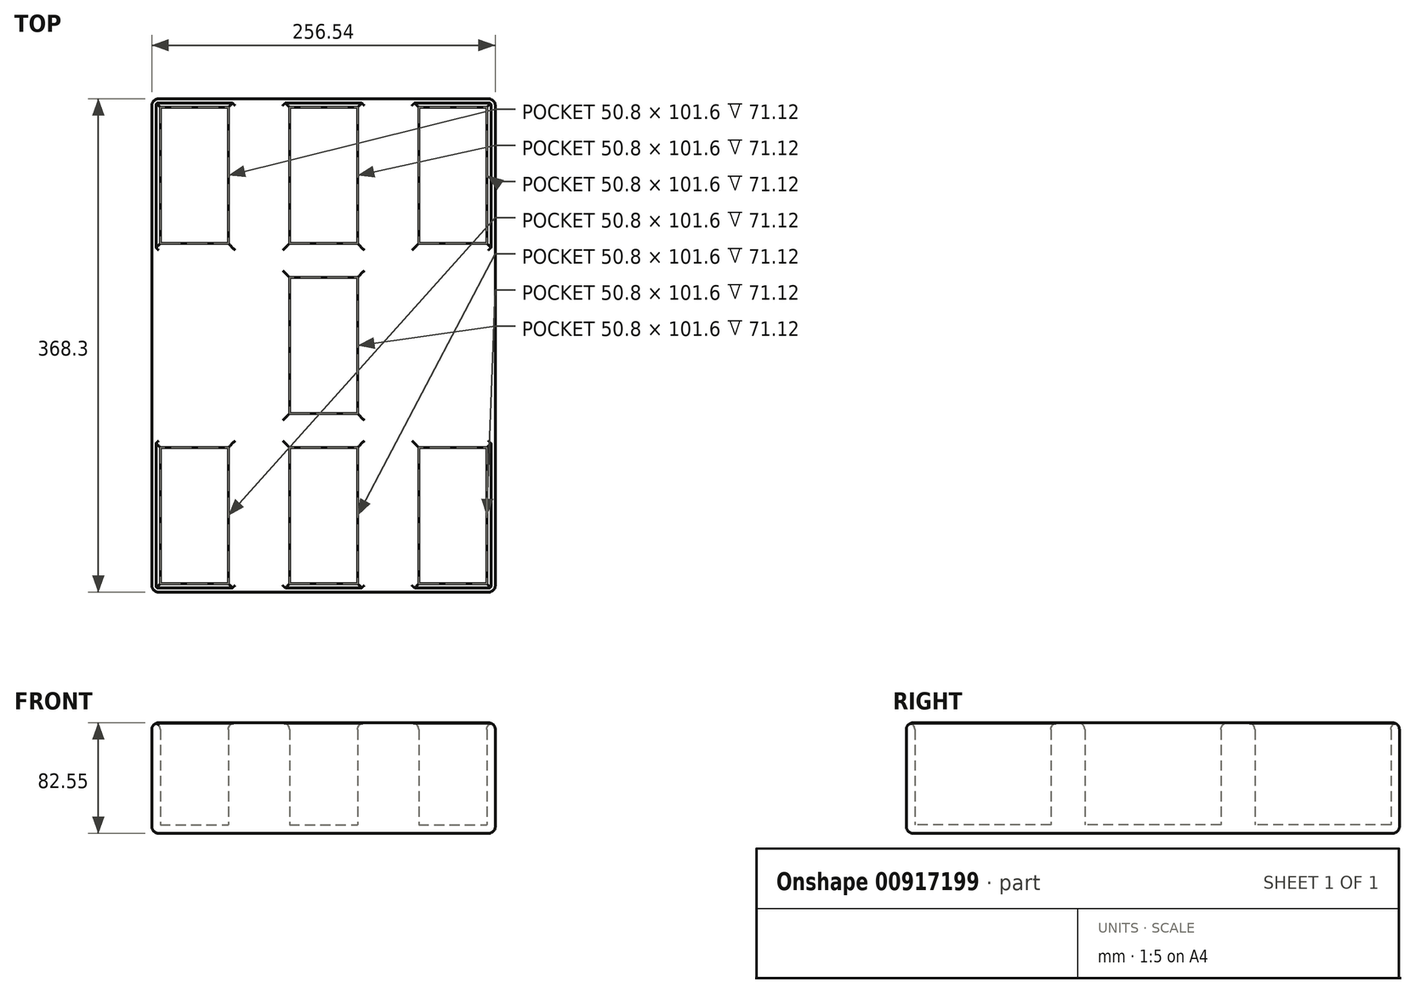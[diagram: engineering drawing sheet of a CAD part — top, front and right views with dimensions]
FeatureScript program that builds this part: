
annotation { "Feature Type Name" : "Feature", "Feature Type Description" : "" }
export const myFeature = defineFeature(function(context is Context, id is Id, definition is map)
    precondition{}
    {
        {
            var Q0;
            Q0=qCreatedBy(makeId("Top.planeOp"),FACE);
            var sketch = newSketch(context, id + "F0", { "sketchPlane" : qUnion([Q0])});
            skLineSegment(sketch, "E0.bottom", {"start": v(-193.27, 101.6) * mm, "end": v(-142.47, 101.6) * mm});
            skLineSegment(sketch, "E0.top", {"start": v(-193.27, 0) * mm, "end": v(-142.47, 0) * mm});
            skLineSegment(sketch, "E0.left", {"start": v(-193.27, 101.6) * mm, "end": v(-193.27, 0) * mm});
            skLineSegment(sketch, "E0.right", {"start": v(-142.47, 101.6) * mm, "end": v(-142.47, 0) * mm});
            skLineSegment(sketch, "E1.bottom", {"start": v(-96.75, 101.6) * mm, "end": v(-45.95, 101.6) * mm});
            skLineSegment(sketch, "E1.top", {"start": v(-96.75, 0) * mm, "end": v(-45.95, 0) * mm});
            skLineSegment(sketch, "E1.left", {"start": v(-96.75, 101.6) * mm, "end": v(-96.75, 0) * mm});
            skLineSegment(sketch, "E1.right", {"start": v(-45.95, 101.6) * mm, "end": v(-45.95, 0) * mm});
            skLineSegment(sketch, "E2.bottom", {"start": v(-0.23, 101.6) * mm, "end": v(50.57, 101.6) * mm});
            skLineSegment(sketch, "E2.top", {"start": v(-0.23, 0) * mm, "end": v(50.57, 0) * mm});
            skLineSegment(sketch, "E2.left", {"start": v(-0.23, 101.6) * mm, "end": v(-0.23, 0) * mm});
            skLineSegment(sketch, "E2.right", {"start": v(50.57, 101.6) * mm, "end": v(50.57, 0) * mm});
            skLineSegment(sketch, "E3.bottom", {"start": v(-193.27, -152.4) * mm, "end": v(-142.47, -152.4) * mm});
            skLineSegment(sketch, "E3.top", {"start": v(-193.27, -254) * mm, "end": v(-142.47, -254) * mm});
            skLineSegment(sketch, "E3.left", {"start": v(-193.27, -152.4) * mm, "end": v(-193.27, -254) * mm});
            skLineSegment(sketch, "E3.right", {"start": v(-142.47, -152.4) * mm, "end": v(-142.47, -254) * mm});
            skLineSegment(sketch, "E4.bottom", {"start": v(-96.75, -152.4) * mm, "end": v(-45.95, -152.4) * mm});
            skLineSegment(sketch, "E4.top", {"start": v(-96.75, -254) * mm, "end": v(-45.95, -254) * mm});
            skLineSegment(sketch, "E4.left", {"start": v(-96.75, -152.4) * mm, "end": v(-96.75, -254) * mm});
            skLineSegment(sketch, "E4.right", {"start": v(-45.95, -152.4) * mm, "end": v(-45.95, -254) * mm});
            skLineSegment(sketch, "E5.bottom", {"start": v(-0.23, -152.4) * mm, "end": v(50.57, -152.4) * mm});
            skLineSegment(sketch, "E5.top", {"start": v(-0.23, -254) * mm, "end": v(50.57, -254) * mm});
            skLineSegment(sketch, "E5.left", {"start": v(-0.23, -152.4) * mm, "end": v(-0.23, -254) * mm});
            skLineSegment(sketch, "E5.right", {"start": v(50.57, -152.4) * mm, "end": v(50.57, -254) * mm});
            skLineSegment(sketch, "E6.bottom", {"start": v(-96.75, -25.4) * mm, "end": v(-45.95, -25.4) * mm});
            skLineSegment(sketch, "E6.top", {"start": v(-96.75, -127) * mm, "end": v(-45.95, -127) * mm});
            skLineSegment(sketch, "E6.left", {"start": v(-96.75, -25.4) * mm, "end": v(-96.75, -127) * mm});
            skLineSegment(sketch, "E6.right", {"start": v(-45.95, -25.4) * mm, "end": v(-45.95, -127) * mm});
            skLineSegment(sketch, "E7.0", {"start": v(-199.62, 107.95) * mm, "end": v(-142.47, 107.95) * mm});
            skLineSegment(sketch, "E7.1", {"start": v(-199.62, 107.95) * mm, "end": v(-199.62, 0) * mm});
            skLineSegment(sketch, "E8.0", {"start": v(-199.62, -260.35) * mm, "end": v(-142.47, -260.35) * mm});
            skLineSegment(sketch, "E8.1", {"start": v(-199.62, -152.4) * mm, "end": v(-199.62, -260.35) * mm});
            skLineSegment(sketch, "E9.0", {"start": v(-0.23, -260.35) * mm, "end": v(56.92, -260.35) * mm});
            skLineSegment(sketch, "E9.1", {"start": v(56.92, -152.4) * mm, "end": v(56.92, -260.35) * mm});
            skLineSegment(sketch, "E10.0", {"start": v(56.92, 107.95) * mm, "end": v(56.92, 12.7) * mm});
            skLineSegment(sketch, "E10.1", {"start": v(-0.23, 107.95) * mm, "end": v(56.92, 107.95) * mm});
            skLineSegment(sketch, "E11", {"start": v(-142.47, 107.95) * mm, "end": v(-0.23, 107.95) * mm});
            skLineSegment(sketch, "E12", {"start": v(-199.62, 0) * mm, "end": v(-199.62, -152.4) * mm});
            skLineSegment(sketch, "E13", {"start": v(-142.47, -260.35) * mm, "end": v(-0.23, -260.35) * mm});
            skLineSegment(sketch, "E14", {"start": v(56.92, 12.7) * mm, "end": v(56.92, -152.4) * mm});
            skSolve(sketch);
        }
        {
            var Q0;
            Q0=makeQuery(id+"F0.imprint","IMPRINT",FACE,{"disambiguationData":[TD([[makeQuery(id+"F0.imprint","IMPRINT",EDGE,{"derivedFrom":sQuery(id+"F0.wireOp",EDGE,"E0.bottom")}),1.0]])]});
            extrude(context, id + "F1", {"entities" : qUnion([Q0]), "depth" : 82.55 * mm, "offsetDistance" : 25.4 * mm});
        }
        {
            var Q0;
            Q0=makeQuery(id+"F0.imprint","IMPRINT",FACE,{"disambiguationData":[TD([[makeQuery(id+"F0.imprint","IMPRINT",EDGE,{"derivedFrom":sQuery(id+"F0.wireOp",EDGE,"E0.bottom")}),-1.0]])]});
            var Q1;
            Q1=makeQuery(id+"F0.imprint","IMPRINT",FACE,{"disambiguationData":[TD([[makeQuery(id+"F0.imprint","IMPRINT",EDGE,{"derivedFrom":sQuery(id+"F0.wireOp",EDGE,"E1.bottom")}),-1.0]])]});
            var Q2;
            Q2=makeQuery(id+"F0.imprint","IMPRINT",FACE,{"disambiguationData":[TD([[makeQuery(id+"F0.imprint","IMPRINT",EDGE,{"derivedFrom":sQuery(id+"F0.wireOp",EDGE,"E2.bottom")}),-1.0]])]});
            var Q3;
            Q3=makeQuery(id+"F0.imprint","IMPRINT",FACE,{"disambiguationData":[TD([[makeQuery(id+"F0.imprint","IMPRINT",EDGE,{"derivedFrom":sQuery(id+"F0.wireOp",EDGE,"E6.bottom")}),-1.0]])]});
            var Q4;
            Q4=makeQuery(id+"F0.imprint","IMPRINT",FACE,{"disambiguationData":[TD([[makeQuery(id+"F0.imprint","IMPRINT",EDGE,{"derivedFrom":sQuery(id+"F0.wireOp",EDGE,"E3.bottom")}),-1.0]])]});
            var Q5;
            Q5=makeQuery(id+"F0.imprint","IMPRINT",FACE,{"disambiguationData":[TD([[makeQuery(id+"F0.imprint","IMPRINT",EDGE,{"derivedFrom":sQuery(id+"F0.wireOp",EDGE,"E4.bottom")}),-1.0]])]});
            var Q6;
            Q6=makeQuery(id+"F0.imprint","IMPRINT",FACE,{"disambiguationData":[TD([[makeQuery(id+"F0.imprint","IMPRINT",EDGE,{"derivedFrom":sQuery(id+"F0.wireOp",EDGE,"E5.bottom")}),-1.0]])]});
            extrude(context, id + "F2", {"entities" : qUnion([Q0, Q1, Q2, Q3, Q4, Q5, Q6]), "operationType" : NewBodyOperationType.ADD, "depth" : 6.35 * mm, "offsetDistance" : 25.4 * mm});
        }
        {
            var Q0;
            Q0=makeQuery(id+"F1.opExtrude","CAP_FACE",FACE,{"disambiguationData":[OSD([sQuery(id+"F0.wireOp",EDGE,"E0.bottom"),sQuery(id+"F0.wireOp",EDGE,"E0.top"),sQuery(id+"F0.wireOp",EDGE,"E0.left"),sQuery(id+"F0.wireOp",EDGE,"E0.right"),sQuery(id+"F0.wireOp",EDGE,"E1.bottom"),sQuery(id+"F0.wireOp",EDGE,"E1.top"),sQuery(id+"F0.wireOp",EDGE,"E1.left"),sQuery(id+"F0.wireOp",EDGE,"E1.right"),sQuery(id+"F0.wireOp",EDGE,"E2.bottom"),sQuery(id+"F0.wireOp",EDGE,"E2.top"),sQuery(id+"F0.wireOp",EDGE,"E2.left"),sQuery(id+"F0.wireOp",EDGE,"E2.right"),sQuery(id+"F0.wireOp",EDGE,"E3.bottom"),sQuery(id+"F0.wireOp",EDGE,"E3.top"),sQuery(id+"F0.wireOp",EDGE,"E3.left"),sQuery(id+"F0.wireOp",EDGE,"E3.right"),sQuery(id+"F0.wireOp",EDGE,"E4.bottom"),sQuery(id+"F0.wireOp",EDGE,"E4.top"),sQuery(id+"F0.wireOp",EDGE,"E4.left"),sQuery(id+"F0.wireOp",EDGE,"E4.right"),sQuery(id+"F0.wireOp",EDGE,"E5.bottom"),sQuery(id+"F0.wireOp",EDGE,"E5.top"),sQuery(id+"F0.wireOp",EDGE,"E5.left"),sQuery(id+"F0.wireOp",EDGE,"E5.right"),sQuery(id+"F0.wireOp",EDGE,"E6.bottom"),sQuery(id+"F0.wireOp",EDGE,"E6.top"),sQuery(id+"F0.wireOp",EDGE,"E6.left"),sQuery(id+"F0.wireOp",EDGE,"E6.right"),sQuery(id+"F0.wireOp",EDGE,"E7.0"),sQuery(id+"F0.wireOp",EDGE,"E7.1"),sQuery(id+"F0.wireOp",EDGE,"E8.0"),sQuery(id+"F0.wireOp",EDGE,"E8.1"),sQuery(id+"F0.wireOp",EDGE,"E9.0"),sQuery(id+"F0.wireOp",EDGE,"E9.1"),sQuery(id+"F0.wireOp",EDGE,"E10.0"),sQuery(id+"F0.wireOp",EDGE,"E10.1"),sQuery(id+"F0.wireOp",EDGE,"E11"),sQuery(id+"F0.wireOp",EDGE,"E12"),sQuery(id+"F0.wireOp",EDGE,"E13"),sQuery(id+"F0.wireOp",EDGE,"E14")])],"isStart":false});
            var Q1;
            {var subQ0=sQuery(id+"F0.wireOp",EDGE,"E6.right");var subQ1=sQuery(id+"F0.wireOp",EDGE,"E6.left");var subQ2=sQuery(id+"F0.wireOp",EDGE,"E6.top");var subQ3=sQuery(id+"F0.wireOp",EDGE,"E6.bottom");var subQ4=sQuery(id+"F0.wireOp",EDGE,"E5.right");var subQ5=sQuery(id+"F0.wireOp",EDGE,"E5.left");var subQ6=sQuery(id+"F0.wireOp",EDGE,"E5.top");var subQ7=sQuery(id+"F0.wireOp",EDGE,"E5.bottom");var subQ8=sQuery(id+"F0.wireOp",EDGE,"E4.right");var subQ9=sQuery(id+"F0.wireOp",EDGE,"E4.left");var subQ10=sQuery(id+"F0.wireOp",EDGE,"E4.top");var subQ11=sQuery(id+"F0.wireOp",EDGE,"E4.bottom");var subQ12=sQuery(id+"F0.wireOp",EDGE,"E3.right");var subQ13=sQuery(id+"F0.wireOp",EDGE,"E3.left");var subQ14=sQuery(id+"F0.wireOp",EDGE,"E3.top");var subQ15=sQuery(id+"F0.wireOp",EDGE,"E3.bottom");var subQ16=sQuery(id+"F0.wireOp",EDGE,"E2.right");var subQ17=sQuery(id+"F0.wireOp",EDGE,"E2.left");var subQ18=sQuery(id+"F0.wireOp",EDGE,"E2.top");var subQ19=sQuery(id+"F0.wireOp",EDGE,"E2.bottom");var subQ20=sQuery(id+"F0.wireOp",EDGE,"E1.right");var subQ21=sQuery(id+"F0.wireOp",EDGE,"E1.left");var subQ22=sQuery(id+"F0.wireOp",EDGE,"E1.top");var subQ23=sQuery(id+"F0.wireOp",EDGE,"E1.bottom");var subQ24=sQuery(id+"F0.wireOp",EDGE,"E0.right");var subQ25=sQuery(id+"F0.wireOp",EDGE,"E0.left");var subQ26=sQuery(id+"F0.wireOp",EDGE,"E0.top");var subQ27=sQuery(id+"F0.wireOp",EDGE,"E0.bottom");Q1=makeQuery(id+"F2.boolean.opBoolean","MERGE",FACE,{"derivedFrom":[makeQuery(id+"F1.opExtrude","CAP_FACE",FACE,{"disambiguationData":[OSD([subQ27,subQ26,subQ25,subQ24,subQ23,subQ22,subQ21,subQ20,subQ19,subQ18,subQ17,subQ16,subQ15,subQ14,subQ13,subQ12,subQ11,subQ10,subQ9,subQ8,subQ7,subQ6,subQ5,subQ4,subQ3,subQ2,subQ1,subQ0,sQuery(id+"F0.wireOp",EDGE,"E7.0"),sQuery(id+"F0.wireOp",EDGE,"E7.1"),sQuery(id+"F0.wireOp",EDGE,"E8.0"),sQuery(id+"F0.wireOp",EDGE,"E8.1"),sQuery(id+"F0.wireOp",EDGE,"E9.0"),sQuery(id+"F0.wireOp",EDGE,"E9.1"),sQuery(id+"F0.wireOp",EDGE,"E10.0"),sQuery(id+"F0.wireOp",EDGE,"E10.1"),sQuery(id+"F0.wireOp",EDGE,"E11"),sQuery(id+"F0.wireOp",EDGE,"E12"),sQuery(id+"F0.wireOp",EDGE,"E13"),sQuery(id+"F0.wireOp",EDGE,"E14")])],"isStart":true}),makeQuery(id+"F2.opExtrude","CAP_FACE",FACE,{"disambiguationData":[OSD([subQ27,subQ26,subQ25,subQ24])],"isStart":true}),makeQuery(id+"F2.opExtrude","CAP_FACE",FACE,{"disambiguationData":[OSD([subQ23,subQ22,subQ21,subQ20])],"isStart":true}),makeQuery(id+"F2.opExtrude","CAP_FACE",FACE,{"disambiguationData":[OSD([subQ19,subQ18,subQ17,subQ16])],"isStart":true}),makeQuery(id+"F2.opExtrude","CAP_FACE",FACE,{"disambiguationData":[OSD([subQ15,subQ14,subQ13,subQ12])],"isStart":true}),makeQuery(id+"F2.opExtrude","CAP_FACE",FACE,{"disambiguationData":[OSD([subQ11,subQ10,subQ9,subQ8])],"isStart":true}),makeQuery(id+"F2.opExtrude","CAP_FACE",FACE,{"disambiguationData":[OSD([subQ7,subQ6,subQ5,subQ4])],"isStart":true}),makeQuery(id+"F2.opExtrude","CAP_FACE",FACE,{"disambiguationData":[OSD([subQ3,subQ2,subQ1,subQ0])],"isStart":true})]});}
            var Q2;
            Q2=makeQuery(id+"F1.opExtrude","SWEPT_EDGE",EDGE,{"disambiguationData":[OSD([sQuery(id+"F0.wireOp",EDGE,"E9.0"),sQuery(id+"F0.wireOp",EDGE,"E9.1")])]});
            var Q3;
            Q3=makeQuery(id+"F1.opExtrude","SWEPT_EDGE",EDGE,{"disambiguationData":[OSD([sQuery(id+"F0.wireOp",EDGE,"E10.0"),sQuery(id+"F0.wireOp",EDGE,"E10.1")])]});
            var Q4;
            Q4=makeQuery(id+"F1.opExtrude","SWEPT_EDGE",EDGE,{"disambiguationData":[OSD([sQuery(id+"F0.wireOp",EDGE,"E7.0"),sQuery(id+"F0.wireOp",EDGE,"E7.1")])]});
            var Q5;
            Q5=makeQuery(id+"F1.opExtrude","SWEPT_EDGE",EDGE,{"disambiguationData":[OSD([sQuery(id+"F0.wireOp",EDGE,"E8.0"),sQuery(id+"F0.wireOp",EDGE,"E8.1")])]});
            fillet(context, id + "F3", {"entities" : qUnion([Q0, Q1, Q2, Q3, Q4, Q5]), "radius" : 5.08 * mm, "tangentPropagation" : true, "allowEdgeOverflow" : false});
        }
    });
